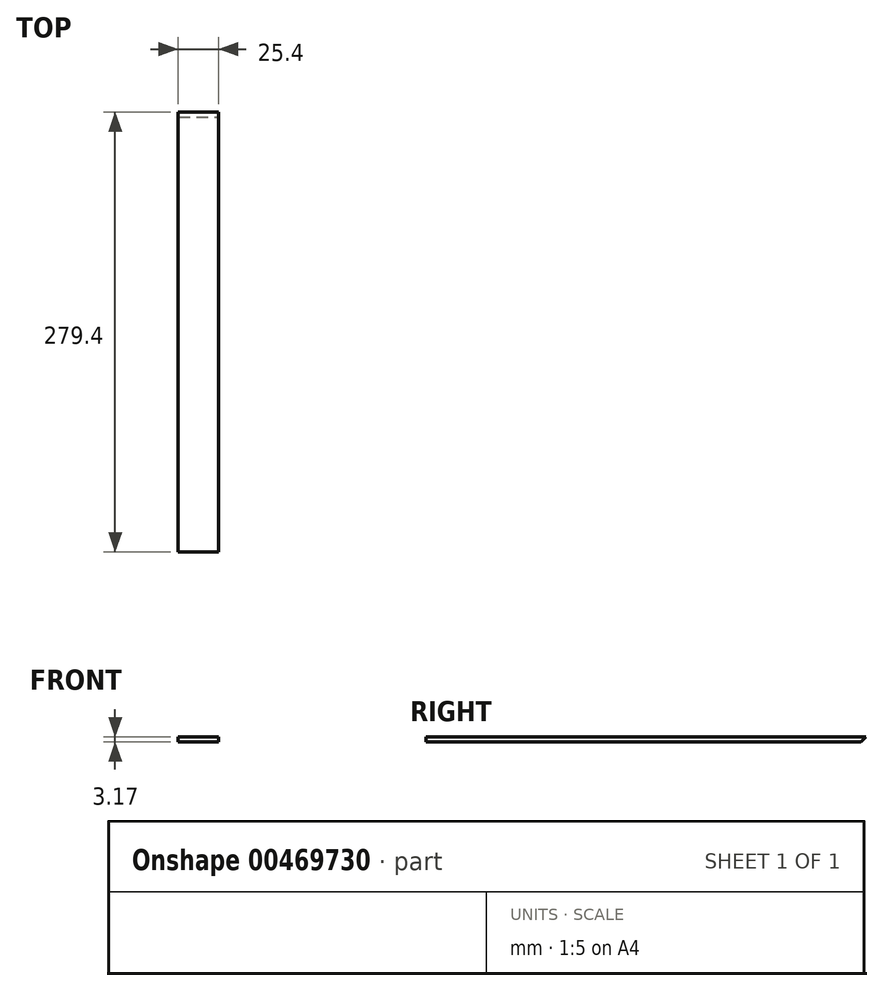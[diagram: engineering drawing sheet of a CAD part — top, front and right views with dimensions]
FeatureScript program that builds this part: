
annotation { "Feature Type Name" : "Feature", "Feature Type Description" : "" }
export const myFeature = defineFeature(function(context is Context, id is Id, definition is map)
    precondition{}
    {
        {
            var Q0;
            Q0=qCreatedBy(makeId("Right.planeOp"),FACE);
            var sketch = newSketch(context, id + "F0", { "sketchPlane" : qUnion([Q0])});
            skLineSegment(sketch, "E0.bottom", {"start": v(0, 0) * mm, "end": v(-279.4, 0) * mm});
            skLineSegment(sketch, "E0.top", {"start": v(0, 3.17) * mm, "end": v(-279.4, 3.17) * mm});
            skLineSegment(sketch, "E0.left", {"start": v(0, 0) * mm, "end": v(0, 3.17) * mm});
            skLineSegment(sketch, "E0.right", {"start": v(-279.4, 0) * mm, "end": v(-279.4, 3.17) * mm});
            skSolve(sketch);
        }
        {
            var Q0;
            Q0=makeQuery(id+"F0.imprint","IMPRINT",FACE,{"disambiguationData":[TD([[makeQuery(id+"F0.imprint","IMPRINT",EDGE,{"derivedFrom":sQuery(id+"F0.wireOp",EDGE,"E0.bottom")}),-1.0]])]});
            extrude(context, id + "F1", {"entities" : qUnion([Q0]), "depth" : 25.4 * mm, "offsetDistance" : 25.4 * mm});
        }
        {
            var Q0;
            Q0=makeQuery(id+"F1.opExtrude","SWEPT_EDGE",EDGE,{"disambiguationData":[OSD([sQuery(id+"F0.wireOp",EDGE,"E0.bottom"),sQuery(id+"F0.wireOp",EDGE,"E0.left")])]});
            chamfer(context, id + "F2", {"entities" : qUnion([Q0]), "width" : 3.17 * mm, "tangentPropagation" : true});
        }
    });
